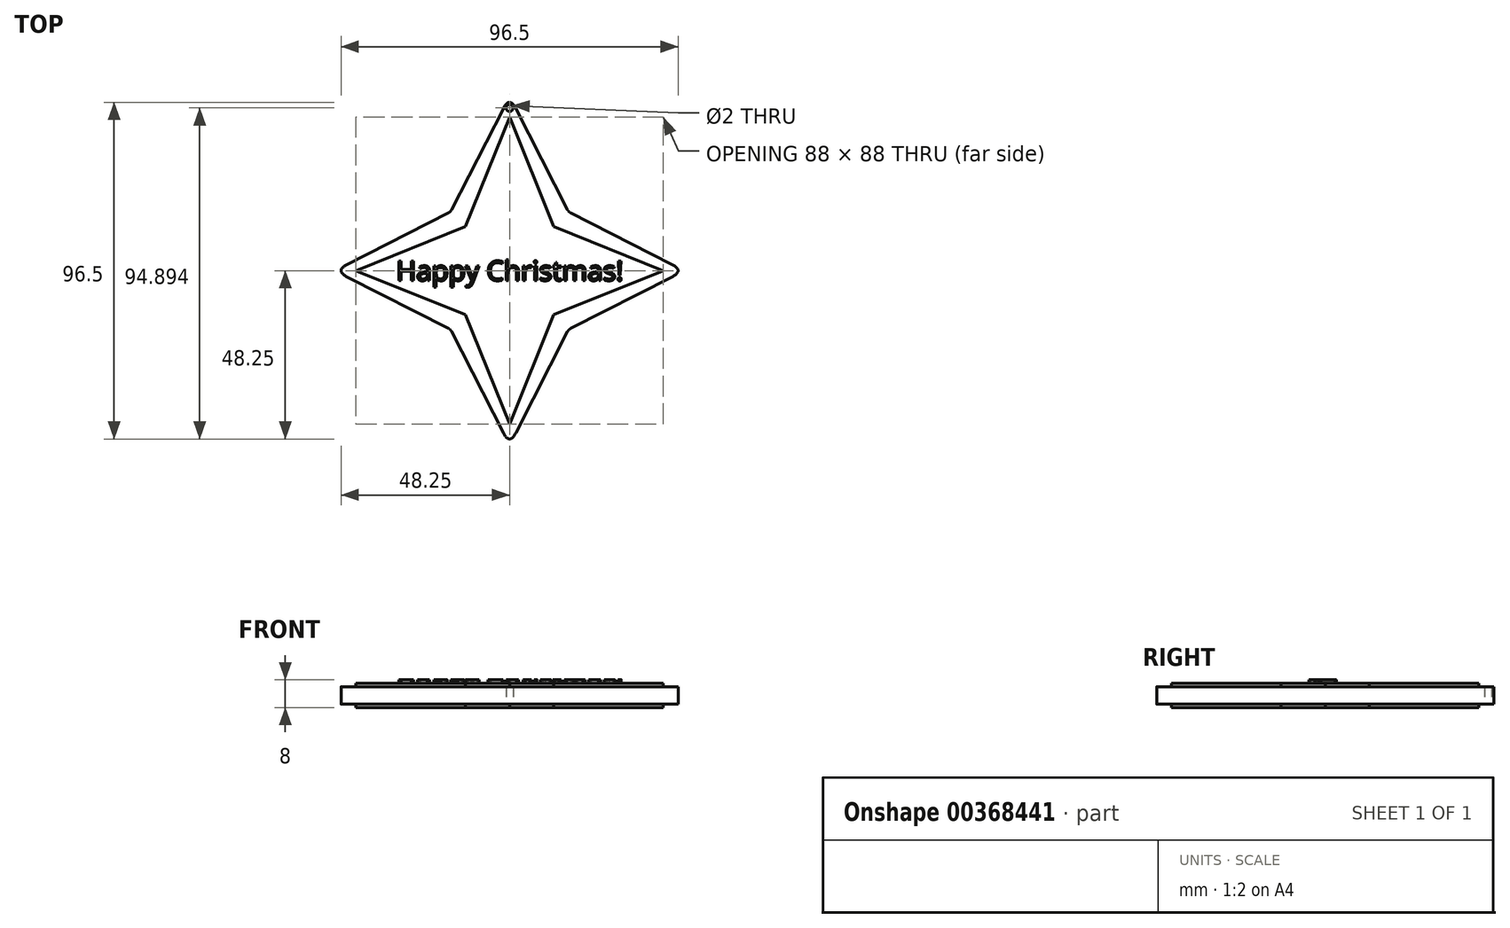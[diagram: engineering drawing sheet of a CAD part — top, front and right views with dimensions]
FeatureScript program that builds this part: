
annotation { "Feature Type Name" : "Feature", "Feature Type Description" : "" }
export const myFeature = defineFeature(function(context is Context, id is Id, definition is map)
    precondition{}
    {
        {
            var Q0;
            Q0=qCreatedBy(makeId("Top.planeOp"),FACE);
            var sketch = newSketch(context, id + "F0", { "sketchPlane" : qUnion([Q0])});
            skLineSegment(sketch, "E0.bottom", {"start": v(50, -50) * mm, "end": v(-50, -50) * mm, "construction": true});
            skLineSegment(sketch, "E0.top", {"start": v(50, 50) * mm, "end": v(-50, 50) * mm, "construction": true});
            skLineSegment(sketch, "E0.left", {"start": v(50, -50) * mm, "end": v(50, 50) * mm, "construction": true});
            skLineSegment(sketch, "E0.right", {"start": v(-50, -50) * mm, "end": v(-50, 50) * mm, "construction": true});
            skPoint(sketch, "E0.middle", {"position": v(0, 0) * mm});
            skLineSegment(sketch, "E1", {"start": v(-50, 50) * mm, "end": v(50, -50) * mm, "construction": true});
            skLineSegment(sketch, "E2", {"start": v(-50, -50) * mm, "end": v(50, 50) * mm, "construction": true});
            skLineSegment(sketch, "E3", {"start": v(0, 50) * mm, "end": v(50, 0) * mm, "construction": true});
            skLineSegment(sketch, "E4", {"start": v(0, 50) * mm, "end": v(-50, 0) * mm, "construction": true});
            skLineSegment(sketch, "E5", {"start": v(-50, 0) * mm, "end": v(0, -50) * mm, "construction": true});
            skLineSegment(sketch, "E6", {"start": v(0, -50) * mm, "end": v(50, 0) * mm, "construction": true});
            skLineSegment(sketch, "E7", {"start": v(0, 50) * mm, "end": v(0, -50) * mm, "construction": true});
            skLineSegment(sketch, "E8", {"start": v(-50, 0) * mm, "end": v(50, 0) * mm, "construction": true});
            skLineSegment(sketch, "E9", {"start": v(0, 50) * mm, "end": v(-16.89, 16.89) * mm});
            skLineSegment(sketch, "E10", {"start": v(-16.89, 16.89) * mm, "end": v(-50, 0) * mm});
            skLineSegment(sketch, "E11", {"start": v(-50, 0) * mm, "end": v(-16.89, -16.89) * mm});
            skLineSegment(sketch, "E12", {"start": v(-16.89, -16.89) * mm, "end": v(0, -50) * mm});
            skLineSegment(sketch, "E13", {"start": v(0, -50) * mm, "end": v(16.89, -16.89) * mm});
            skLineSegment(sketch, "E14", {"start": v(16.89, -16.89) * mm, "end": v(50, 0) * mm});
            skLineSegment(sketch, "E15", {"start": v(50, 0) * mm, "end": v(16.89, 16.89) * mm});
            skLineSegment(sketch, "E16", {"start": v(16.89, 16.89) * mm, "end": v(0, 50) * mm});
            skLineSegment(sketch, "E17", {"start": v(0, 44) * mm, "end": v(-12.65, 12.65) * mm});
            skLineSegment(sketch, "E18", {"start": v(-12.65, 12.65) * mm, "end": v(-44, 0) * mm});
            skLineSegment(sketch, "E19", {"start": v(-44, 0) * mm, "end": v(-12.65, -12.65) * mm});
            skLineSegment(sketch, "E20", {"start": v(-12.65, -12.65) * mm, "end": v(0, -44) * mm});
            skLineSegment(sketch, "E21", {"start": v(0, -44) * mm, "end": v(12.65, -12.65) * mm});
            skLineSegment(sketch, "E22", {"start": v(12.65, -12.65) * mm, "end": v(44, 0) * mm});
            skLineSegment(sketch, "E23", {"start": v(44, 0) * mm, "end": v(12.65, 12.65) * mm});
            skLineSegment(sketch, "E24", {"start": v(12.65, 12.65) * mm, "end": v(0, 44) * mm});
            skPoint(sketch, "E25.0", {"position": v(0, 50) * mm});
            skPoint(sketch, "E26.0", {"position": v(50, 0) * mm});
            skPoint(sketch, "E27.0", {"position": v(0, -50) * mm});
            skPoint(sketch, "E28.0", {"position": v(-50, 0) * mm});
            skPoint(sketch, "E29.orphan", {"position": v(-49.57, 0) * mm});
            skPoint(sketch, "E30.orphan", {"position": v(50.4, 0) * mm});
            skPoint(sketch, "E31.0", {"position": v(16.89, 16.89) * mm});
            skPoint(sketch, "E31.1", {"position": v(-16.89, 16.89) * mm});
            skPoint(sketch, "E31.2", {"position": v(16.89, -16.89) * mm});
            skPoint(sketch, "E31.3", {"position": v(-16.89, -16.89) * mm});
            skCircle(sketch, "E32", {"center": v(0, 46.64) * mm, "radius": 1 * mm});
            skSolve(sketch);
        }
        {
            var Q0;
            Q0=makeQuery(id+"F0.imprint","IMPRINT",FACE,{"disambiguationData":[TD([[makeQuery(id+"F0.imprint","IMPRINT",EDGE,{"derivedFrom":sQuery(id+"F0.wireOp",EDGE,"E9")}),1.0]])]});
            var Q1;
            Q1=makeQuery(id+"F0.imprint","IMPRINT",FACE,{"disambiguationData":[TD([[makeQuery(id+"F0.imprint","IMPRINT",EDGE,{"derivedFrom":sQuery(id+"F0.wireOp",EDGE,"E17")}),1.0]])]});
            extrude(context, id + "F1", {"entities" : qUnion([Q0, Q1]), "depth" : 5 * mm});
        }
        {
            var Q0;
            Q0=makeQuery(id+"F0.imprint","IMPRINT",FACE,{"disambiguationData":[TD([[makeQuery(id+"F0.imprint","IMPRINT",EDGE,{"derivedFrom":sQuery(id+"F0.wireOp",EDGE,"E17")}),1.0]])]});
            extrude(context, id + "F2", {"entities" : qUnion([Q0]), "operationType" : NewBodyOperationType.ADD, "depth" : 6 * mm});
        }
        {
            var Q0;
            Q0=makeQuery(id+"F0.imprint","IMPRINT",FACE,{"disambiguationData":[TD([[makeQuery(id+"F0.imprint","IMPRINT",EDGE,{"derivedFrom":sQuery(id+"F0.wireOp",EDGE,"E17")}),1.0]])]});
            extrude(context, id + "F3", {"entities" : qUnion([Q0]), "operationType" : NewBodyOperationType.ADD, "oppositeDirection" : true, "depth" : 1 * mm});
        }
        {
            var Q0;
            Q0=makeQuery(id+"F1.opExtrude","SWEPT_EDGE",EDGE,{"disambiguationData":[OSD([sQuery(id+"F0.wireOp",EDGE,"E12"),sQuery(id+"F0.wireOp",EDGE,"E13")])]});
            var Q1;
            Q1=makeQuery(id+"F1.opExtrude","SWEPT_EDGE",EDGE,{"disambiguationData":[OSD([sQuery(id+"F0.wireOp",EDGE,"E15"),sQuery(id+"F0.wireOp",EDGE,"E16")])]});
            var Q2;
            Q2=makeQuery(id+"F1.opExtrude","SWEPT_EDGE",EDGE,{"disambiguationData":[OSD([sQuery(id+"F0.wireOp",EDGE,"E9"),sQuery(id+"F0.wireOp",EDGE,"E16")])]});
            var Q3;
            Q3=makeQuery(id+"F1.opExtrude","SWEPT_EDGE",EDGE,{"disambiguationData":[OSD([sQuery(id+"F0.wireOp",EDGE,"E11"),sQuery(id+"F0.wireOp",EDGE,"E12")])]});
            var Q4;
            Q4=makeQuery(id+"F1.opExtrude","SWEPT_EDGE",EDGE,{"disambiguationData":[OSD([sQuery(id+"F0.wireOp",EDGE,"E14"),sQuery(id+"F0.wireOp",EDGE,"E15")])]});
            var Q5;
            Q5=makeQuery(id+"F1.opExtrude","SWEPT_EDGE",EDGE,{"disambiguationData":[OSD([sQuery(id+"F0.wireOp",EDGE,"E9"),sQuery(id+"F0.wireOp",EDGE,"E10")])]});
            var Q6;
            Q6=makeQuery(id+"F1.opExtrude","SWEPT_EDGE",EDGE,{"disambiguationData":[OSD([sQuery(id+"F0.wireOp",EDGE,"E13"),sQuery(id+"F0.wireOp",EDGE,"E14")])]});
            var Q7;
            Q7=makeQuery(id+"F1.opExtrude","SWEPT_EDGE",EDGE,{"disambiguationData":[OSD([sQuery(id+"F0.wireOp",EDGE,"E10"),sQuery(id+"F0.wireOp",EDGE,"E11")])]});
            fillet(context, id + "F4", {"entities" : qUnion([Q0, Q1, Q2, Q3, Q4, Q5, Q6, Q7]), "radius" : 2 * mm, "tangentPropagation" : true, "rho" : 0.5, "crossSection" : FilletCrossSection.CONIC, "allowEdgeOverflow" : false});
        }
        {
            var Q0;
            Q0=makeQuery(id+"F2.opExtrude","CAP_FACE",FACE,{"disambiguationData":[OSD([sQuery(id+"F0.wireOp",EDGE,"E17"),sQuery(id+"F0.wireOp",EDGE,"E18"),sQuery(id+"F0.wireOp",EDGE,"E19"),sQuery(id+"F0.wireOp",EDGE,"E20"),sQuery(id+"F0.wireOp",EDGE,"E21"),sQuery(id+"F0.wireOp",EDGE,"E22"),sQuery(id+"F0.wireOp",EDGE,"E23"),sQuery(id+"F0.wireOp",EDGE,"E24")])],"isStart":false});
            var sketch = newSketch(context, id + "F5", { "sketchPlane" : qUnion([Q0])});
            skText(sketch, "E33", { "text": "Happy Christmas!", "fontName": "OpenSans-Regular.ttf"});
            skPoint(sketch, "E34", {"position": v(0, 0) * mm});
            const initialGuessF5  = {"E33": [-0.0325, -0.00284, 1, 0, 0.00568]};
            skSetInitialGuess(sketch, initialGuessF5);
            skSolve(sketch);
        }
        {
            var Q0;
            Q0=makeQuery(id+"F5.imprint","IMPRINT",FACE,{"disambiguationData":[TD([[makeQuery(id+"F5.imprint","IMPRINT",EDGE,{"derivedFrom":sQuery(id+"F5.wireOp",EDGE,"E33.sketch_text.stroke-235")}),-1.0]])]});
            var Q1;
            Q1=makeQuery(id+"F5.imprint","IMPRINT",FACE,{"disambiguationData":[TD([[makeQuery(id+"F5.imprint","IMPRINT",EDGE,{"derivedFrom":sQuery(id+"F5.wireOp",EDGE,"E33.sketch_text.stroke-262")}),-1.0]])]});
            var Q2;
            Q2=makeQuery(id+"F5.imprint","IMPRINT",FACE,{"disambiguationData":[TD([[makeQuery(id+"F5.imprint","IMPRINT",EDGE,{"derivedFrom":sQuery(id+"F5.wireOp",EDGE,"E33.sketch_text.stroke-89")}),-1.0]])]});
            var Q3;
            Q3=makeQuery(id+"F5.imprint","IMPRINT",FACE,{"disambiguationData":[TD([[makeQuery(id+"F5.imprint","IMPRINT",EDGE,{"derivedFrom":sQuery(id+"F5.wireOp",EDGE,"E33.sketch_text.stroke-64")}),-1.0]])]});
            var Q4;
            Q4=makeQuery(id+"F5.imprint","IMPRINT",FACE,{"disambiguationData":[TD([[makeQuery(id+"F5.imprint","IMPRINT",EDGE,{"derivedFrom":sQuery(id+"F5.wireOp",EDGE,"E33.sketch_text.stroke-287")}),-1.0]])]});
            var Q5;
            Q5=makeQuery(id+"F5.imprint","IMPRINT",FACE,{"disambiguationData":[TD([[makeQuery(id+"F5.imprint","IMPRINT",EDGE,{"derivedFrom":sQuery(id+"F5.wireOp",EDGE,"E33.sketch_text.stroke-188")}),-1.0]])]});
            var Q6;
            Q6=makeQuery(id+"F5.imprint","IMPRINT",FACE,{"disambiguationData":[TD([[makeQuery(id+"F5.imprint","IMPRINT",EDGE,{"derivedFrom":sQuery(id+"F5.wireOp",EDGE,"E33.sketch_text.stroke-39")}),-1.0]])]});
            var Q7;
            Q7=makeQuery(id+"F5.imprint","IMPRINT",FACE,{"disambiguationData":[TD([[makeQuery(id+"F5.imprint","IMPRINT",EDGE,{"derivedFrom":sQuery(id+"F5.wireOp",EDGE,"E33.sketch_text.stroke-163")}),-1.0]])]});
            var Q8;
            Q8=makeQuery(id+"F5.imprint","IMPRINT",FACE,{"disambiguationData":[TD([[makeQuery(id+"F5.imprint","IMPRINT",EDGE,{"derivedFrom":sQuery(id+"F5.wireOp",EDGE,"E33.sketch_text.stroke-291")}),-1.0]])]});
            var Q9;
            Q9=makeQuery(id+"F5.imprint","IMPRINT",FACE,{"disambiguationData":[TD([[makeQuery(id+"F5.imprint","IMPRINT",EDGE,{"derivedFrom":sQuery(id+"F5.wireOp",EDGE,"E33.sketch_text.stroke-207")}),-1.0]])]});
            var Q10;
            Q10=makeQuery(id+"F5.imprint","IMPRINT",FACE,{"disambiguationData":[TD([[makeQuery(id+"F5.imprint","IMPRINT",EDGE,{"derivedFrom":sQuery(id+"F5.wireOp",EDGE,"E33.sketch_text.stroke-120")}),-1.0]])]});
            var Q11;
            Q11=makeQuery(id+"F5.imprint","IMPRINT",FACE,{"disambiguationData":[TD([[makeQuery(id+"F5.imprint","IMPRINT",EDGE,{"derivedFrom":sQuery(id+"F5.wireOp",EDGE,"E33.sketch_text.stroke-12")}),-1.0]])]});
            var Q12;
            Q12=makeQuery(id+"F5.imprint","IMPRINT",FACE,{"disambiguationData":[TD([[makeQuery(id+"F5.imprint","IMPRINT",EDGE,{"derivedFrom":sQuery(id+"F5.wireOp",EDGE,"E33.sketch_text.stroke-105")}),-1.0]])]});
            var Q13;
            Q13=makeQuery(id+"F5.imprint","IMPRINT",FACE,{"disambiguationData":[TD([[makeQuery(id+"F5.imprint","IMPRINT",EDGE,{"derivedFrom":sQuery(id+"F5.wireOp",EDGE,"E33.sketch_text.stroke-0")}),-1.0]])]});
            var Q14;
            Q14=makeQuery(id+"F5.imprint","IMPRINT",FACE,{"disambiguationData":[TD([[makeQuery(id+"F5.imprint","IMPRINT",EDGE,{"derivedFrom":sQuery(id+"F5.wireOp",EDGE,"E33.sketch_text.stroke-138")}),-1.0]])]});
            var Q15;
            Q15=makeQuery(id+"F5.imprint","IMPRINT",FACE,{"disambiguationData":[TD([[makeQuery(id+"F5.imprint","IMPRINT",EDGE,{"derivedFrom":sQuery(id+"F5.wireOp",EDGE,"E33.sketch_text.stroke-151")}),-1.0]])]});
            var Q16;
            Q16=makeQuery(id+"F5.imprint","IMPRINT",FACE,{"disambiguationData":[TD([[makeQuery(id+"F5.imprint","IMPRINT",EDGE,{"derivedFrom":sQuery(id+"F5.wireOp",EDGE,"E33.sketch_text.stroke-155")}),-1.0]])]});
            extrude(context, id + "F6", {"entities" : qUnion([Q0, Q1, Q2, Q3, Q4, Q5, Q6, Q7, Q8, Q9, Q10, Q11, Q12, Q13, Q14, Q15, Q16]), "operationType" : NewBodyOperationType.ADD, "depth" : 1 * mm});
        }
    });
